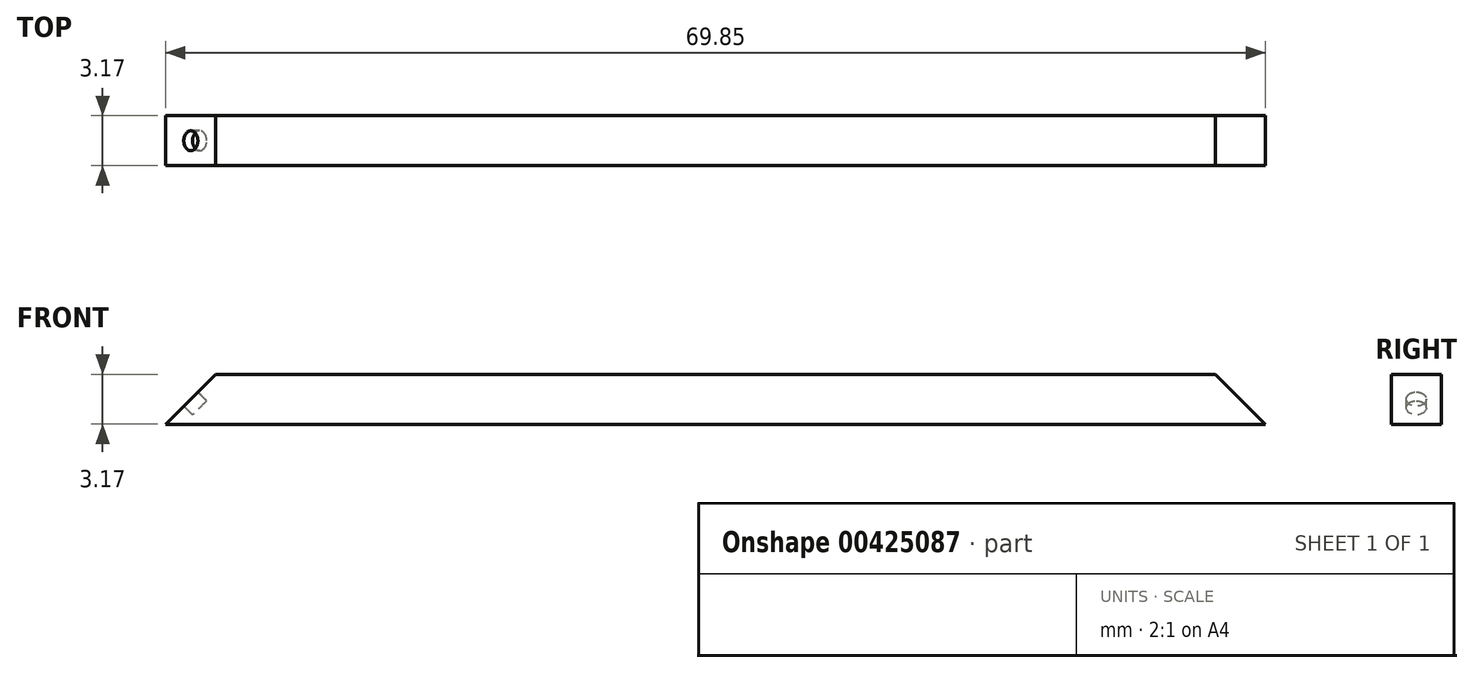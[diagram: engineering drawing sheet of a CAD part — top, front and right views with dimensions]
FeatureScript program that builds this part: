
annotation { "Feature Type Name" : "Feature", "Feature Type Description" : "" }
export const myFeature = defineFeature(function(context is Context, id is Id, definition is map)
    precondition{}
    {
        {
            var Q0;
            Q0=qCreatedBy(makeId("Front.planeOp"),FACE);
            var sketch = newSketch(context, id + "F0", { "sketchPlane" : qUnion([Q0])});
            skLineSegment(sketch, "E0", {"start": v(-39.56, -19.28) * mm, "end": v(27.12, -19.28) * mm});
            skLineSegment(sketch, "E1", {"start": v(27.12, -16.1) * mm, "end": v(-36.38, -16.1) * mm});
            skLineSegment(sketch, "E2", {"start": v(-36.38, -16.1) * mm, "end": v(-39.56, -19.28) * mm});
            skLineSegment(sketch, "E3", {"start": v(27.12, -19.28) * mm, "end": v(27.12, -16.1) * mm});
            skLineSegment(sketch, "E4", {"start": v(27.12, -19.28) * mm, "end": v(30.3, -19.28) * mm});
            skLineSegment(sketch, "E5", {"start": v(30.3, -19.28) * mm, "end": v(27.12, -16.1) * mm});
            skSolve(sketch);
        }
        {
            var Q0;
            Q0 = qSketchRegion(id + "F0", true);
            extrude(context, id + "F1", {"entities" : qUnion([Q0]), "depth" : 3.17 * mm});
        }
        {
            var Q0;
            Q0=makeQuery(id+"F1.opExtrude","SWEPT_FACE",FACE,{"disambiguationData":[OSD([sQuery(id+"F0.wireOp",EDGE,"E2")])]});
            var sketch = newSketch(context, id + "F2", { "sketchPlane" : qUnion([Q0])});
            skCircle(sketch, "E6", {"center": v(1.59, -39.35) * mm, "radius": 0.64 * mm});
            skSolve(sketch);
        }
        {
            var Q0;
            Q0 = qSketchRegion(id + "F2", true);
            extrude(context, id + "F3", {"entities" : qUnion([Q0]), "operationType" : NewBodyOperationType.REMOVE, "oppositeDirection" : true, "depth" : 0.79 * mm});
        }
        {
            var Q0;
            Q0=makeQuery(id+"F1.opExtrude","SWEPT_FACE",FACE,{"disambiguationData":[OSD([sQuery(id+"F0.wireOp",EDGE,"E5")])]});
            var sketch = newSketch(context, id + "F4", { "sketchPlane" : qUnion([Q0])});
            skCircle(sketch, "E7", {"center": v(-1.59, -4.76) * mm, "radius": 0.64 * mm});
            skCircle(sketch, "E8", {"center": v(32.82, -1.59) * mm, "radius": 0.64 * mm});
            skSolve(sketch);
        }
        {
            var Q0;
            Q0=makeQuery(id+"F4.imprint","IMPRINT",FACE,{"disambiguationData":[TD([[makeQuery(id+"F4.imprint","IMPRINT",EDGE,{"derivedFrom":sQuery(id+"F4.wireOp",EDGE,"E8")}),1.0]])]});
            extrude(context, id + "F5", {"entities" : qUnion([Q0]), "operationType" : NewBodyOperationType.REMOVE, "oppositeDirection" : true, "depth" : 0.89 * mm});
        }
    });
